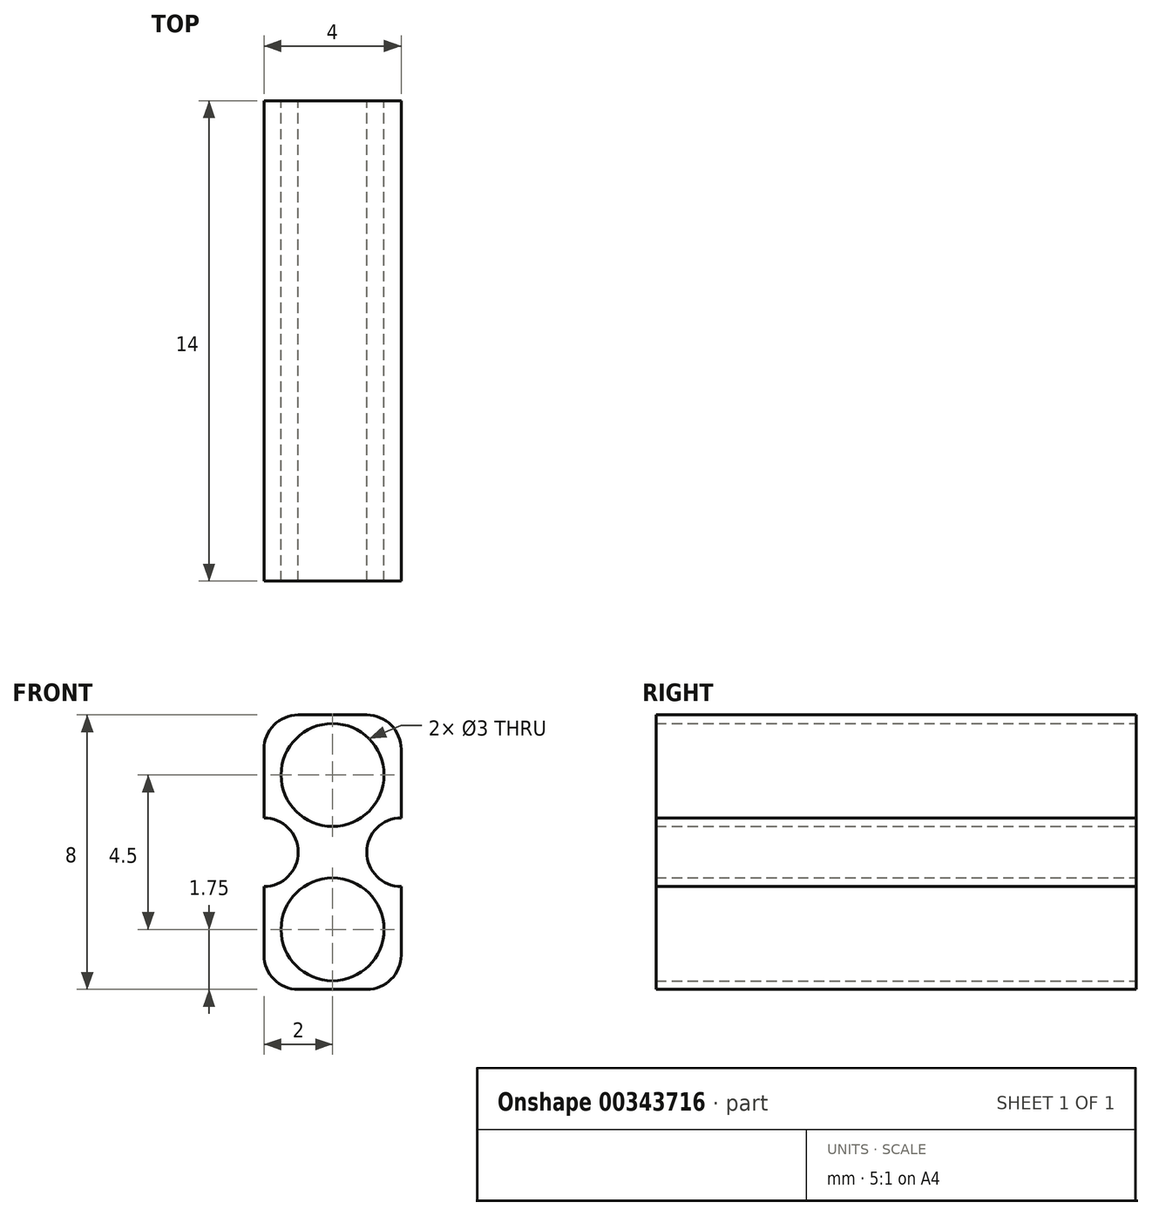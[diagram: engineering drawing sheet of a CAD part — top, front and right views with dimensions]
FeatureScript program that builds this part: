
annotation { "Feature Type Name" : "Feature", "Feature Type Description" : "" }
export const myFeature = defineFeature(function(context is Context, id is Id, definition is map)
    precondition{}
    {
        {
            var Q0;
            Q0=qCreatedBy(makeId("Front.planeOp"),FACE);
            var sketch = newSketch(context, id + "F0", { "sketchPlane" : qUnion([Q0])});
            skLineSegment(sketch, "E0.bottom", {"start": v(1, 0) * mm, "end": v(3, 0) * mm});
            skLineSegment(sketch, "E0.top", {"start": v(1, 8) * mm, "end": v(3, 8) * mm});
            skLineSegment(sketch, "E0.left", {"start": v(0, 1) * mm, "end": v(0, 3) * mm});
            skLineSegment(sketch, "E0.right", {"start": v(4, 1) * mm, "end": v(4, 3) * mm});
            skPoint(sketch, "E1.visualSharp", {"position": v(4, 8) * mm});
            skArc(sketch, "E1.filletArc", {"start": v(4, 7) * mm, "mid": v(3.7, 7.7) * mm, "end": v(3, 8) * mm});
            skPoint(sketch, "E2.visualSharp", {"position": v(0, 8) * mm});
            skArc(sketch, "E2.filletArc", {"start": v(1, 8) * mm, "mid": v(0.3, 7.7) * mm, "end": v(0, 7) * mm});
            skPoint(sketch, "E3.visualSharp", {"position": v(0, 0) * mm});
            skArc(sketch, "E3.filletArc", {"start": v(0, 1) * mm, "mid": v(0.3, 0.3) * mm, "end": v(1, 0) * mm});
            skPoint(sketch, "E4.visualSharp", {"position": v(4, 0) * mm});
            skArc(sketch, "E4.filletArc", {"start": v(3, 0) * mm, "mid": v(3.7, 0.3) * mm, "end": v(4, 1) * mm});
            skLineSegment(sketch, "E5.bottom", {"start": v(0, 5) * mm, "end": v(0, 5) * mm});
            skLineSegment(sketch, "E5.top", {"start": v(0, 3) * mm, "end": v(0, 3) * mm});
            skLineSegment(sketch, "E5.right", {"start": v(1, 4) * mm, "end": v(1, 4) * mm});
            skLineSegment(sketch, "E6.bottom", {"start": v(4, 5) * mm, "end": v(4, 5) * mm});
            skLineSegment(sketch, "E6.top", {"start": v(4, 3) * mm, "end": v(4, 3) * mm});
            skLineSegment(sketch, "E6.right", {"start": v(3, 4) * mm, "end": v(3, 4) * mm});
            skPoint(sketch, "E7.visualSharp", {"position": v(1, 5) * mm});
            skArc(sketch, "E7.filletArc", {"start": v(1, 4) * mm, "mid": v(0.7, 4.7) * mm, "end": v(0, 5) * mm});
            skPoint(sketch, "E8.visualSharp", {"position": v(1, 3) * mm});
            skArc(sketch, "E8.filletArc", {"start": v(0, 3) * mm, "mid": v(0.7, 3.3) * mm, "end": v(1, 4) * mm});
            skPoint(sketch, "E9.visualSharp", {"position": v(3, 3) * mm});
            skArc(sketch, "E9.filletArc", {"start": v(3, 4) * mm, "mid": v(3.3, 3.3) * mm, "end": v(4, 3) * mm});
            skPoint(sketch, "E10.visualSharp", {"position": v(3, 5) * mm});
            skArc(sketch, "E10.filletArc", {"start": v(4, 5) * mm, "mid": v(3.3, 4.7) * mm, "end": v(3, 4) * mm});
            skLineSegment(sketch, "E11.trimOffspring", {"start": v(0, 5) * mm, "end": v(0, 7) * mm});
            skLineSegment(sketch, "E12.trimOffspring", {"start": v(4, 5) * mm, "end": v(4, 7) * mm});
            skPoint(sketch, "E13.visualSharp", {"position": v(1, 4) * mm});
            skSolve(sketch);
        }
        {
            var Q0;
            Q0 = qSketchRegion(id + "F0", true);
            extrude(context, id + "F1", {"entities" : qUnion([Q0]), "depth" : 14 * mm, "offsetDistance" : 25.4 * mm});
        }
        {
            var Q0;
            Q0=qCreatedBy(makeId("Front.planeOp"),FACE);
            var sketch = newSketch(context, id + "F2", { "sketchPlane" : qUnion([Q0])});
            skArc(sketch, "E14", {"start": v(2.47, 4.83) * mm, "mid": v(2, 7.75) * mm, "end": v(1.53, 4.83) * mm});
            skArc(sketch, "E15", {"start": v(1.53, 3.17) * mm, "mid": v(2, 0.25) * mm, "end": v(2.47, 3.17) * mm});
            skLineSegment(sketch, "E16", {"start": v(2.47, 4.83) * mm, "end": v(2.47, 3.17) * mm});
            skLineSegment(sketch, "E17", {"start": v(1.53, 4.83) * mm, "end": v(1.53, 3.17) * mm});
            skLineSegment(sketch, "E18", {"start": v(2.47, 4.83) * mm, "end": v(1.53, 4.83) * mm});
            skLineSegment(sketch, "E19", {"start": v(1.53, 3.17) * mm, "end": v(2.47, 3.17) * mm});
            skSolve(sketch);
        }
        {
            var Q0;
            Q0=sQuery(id+"F2.wireOp",VERTEX,"E14.center");
            var Q1;
            Q1=sQuery(id+"F2.wireOp",VERTEX,"E15.center");
            var Q2;
            Q2=makeQuery(id+"F1.opExtrude","SWEPT_BODY",BODY,{"disambiguationData":[OSD([sQuery(id+"F0.wireOp",EDGE,"E0.bottom"),sQuery(id+"F0.wireOp",EDGE,"E0.top"),sQuery(id+"F0.wireOp",EDGE,"E0.left"),sQuery(id+"F0.wireOp",EDGE,"E0.right"),sQuery(id+"F0.wireOp",EDGE,"E1.filletArc"),sQuery(id+"F0.wireOp",EDGE,"E2.filletArc"),sQuery(id+"F0.wireOp",EDGE,"E3.filletArc"),sQuery(id+"F0.wireOp",EDGE,"E4.filletArc"),sQuery(id+"F0.wireOp",EDGE,"E7.filletArc"),sQuery(id+"F0.wireOp",EDGE,"E8.filletArc"),sQuery(id+"F0.wireOp",EDGE,"E9.filletArc"),sQuery(id+"F0.wireOp",EDGE,"E10.filletArc"),sQuery(id+"F0.wireOp",EDGE,"E11.trimOffspring"),sQuery(id+"F0.wireOp",EDGE,"E12.trimOffspring")])]});
            hole(context, id + "F3", {"style" : HoleStyle.SIMPLE, "endStyle" : HoleEndStyle.THROUGH, "oppositeDirection" : true, "holeDiameter" : 3 * mm, "isTappedThrough" : true, "tappedDepth" : 12.7 * mm, "tapClearance" : 3, "locations" : qUnion([Q0, Q1]), "scope" : qUnion([Q2]), "majorDiameter" : 6.35 * mm});
        }
    });
